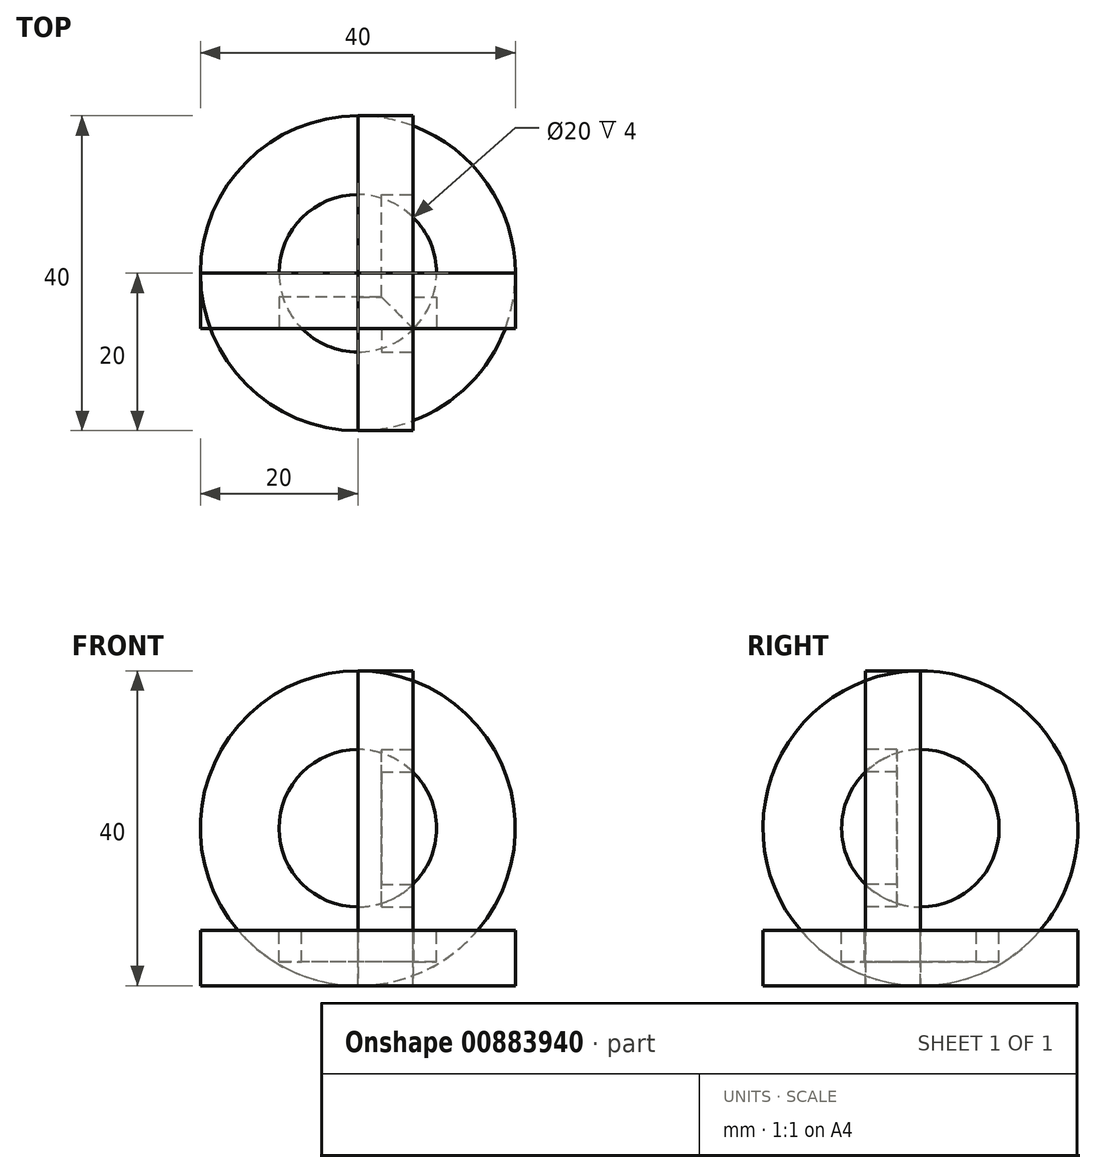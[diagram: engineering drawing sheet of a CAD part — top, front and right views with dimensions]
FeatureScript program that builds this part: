
annotation { "Feature Type Name" : "Feature", "Feature Type Description" : "" }
export const myFeature = defineFeature(function(context is Context, id is Id, definition is map)
    precondition{}
    {
        {
            assignVariable(context, id + "F0", {"name" : "outer_high", "anyValue" : 7});
        }
        {
            assignVariable(context, id + "F1", {"name" : "inner_high", "anyValue" : 4});
        }
        {
            assignVariable(context, id + "F2", {"name" : "column_angle", "anyValue" : 90});
        }
        {
            var Q0;
            Q0=qCreatedBy(makeId("Top.planeOp"),FACE);
            var sketch = newSketch(context, id + "F3", { "sketchPlane" : qUnion([Q0])});
            skCircle(sketch, "E0", {"center": v(0, 0) * mm, "radius": 20 * mm});
            skCircle(sketch, "E1", {"center": v(0, 0) * mm, "radius": 10 * mm});
            skSolve(sketch);
        }
        {
            var Q0;
            Q0=makeQuery(id+"F3.imprint","IMPRINT",FACE,{"disambiguationData":[TD([[makeQuery(id+"F3.imprint","IMPRINT",EDGE,{"derivedFrom":sQuery(id+"F3.wireOp",EDGE,"E0")}),1.0]])]});
            var Q1;
            Q1=makeQuery(id+"F3.imprint","IMPRINT",FACE,{"disambiguationData":[TD([[makeQuery(id+"F3.imprint","IMPRINT",EDGE,{"derivedFrom":sQuery(id+"F3.wireOp",EDGE,"E1")}),1.0]])]});
            extrude(context, id + "F4", {"entities" : qUnion([Q0, Q1]), "depth" : (getVariable(context, 'outer_high')) * mm, "offsetDistance" : 25 * mm});
        }
        {
            var Q0;
            Q0=makeQuery(id+"F4.opExtrude","CAP_FACE",FACE,{"disambiguationData":[OSD([sQuery(id+"F3.wireOp",EDGE,"E0")])],"isStart":false});
            var sketch = newSketch(context, id + "F5", { "sketchPlane" : qUnion([Q0])});
            skCircle(sketch, "E2.0", {"center": v(0, 0) * mm, "radius": 10 * mm});
            skSolve(sketch);
        }
        {
            var Q0;
            Q0=qCreatedBy(makeId("Front.planeOp"),FACE);
            var sketch = newSketch(context, id + "F6", { "sketchPlane" : qUnion([Q0])});
            skLineSegment(sketch, "E3", {"start": v(0, 70) * mm, "end": v(0, 0) * mm});
            skPoint(sketch, "E4", {"position": v(0, 20) * mm});
            skCircle(sketch, "E5", {"center": v(0, 20) * mm, "radius": 20 * mm});
            skCircle(sketch, "E6", {"center": v(0, 20) * mm, "radius": 10 * mm});
            skSolve(sketch);
        }
        {
            var Q0;
            {var subQ0=sQuery(id+"F6.wireOp",EDGE,"E5");var subQ1=sQuery(id+"F6.wireOp",EDGE,"E3");var subQ2=makeQuery(id+"F6.imprint","INTERSECT",VERTEX,{"disambiguationData":[OD(1.0)],"derivedFrom":[subQ1,subQ0]});Q0=makeQuery(id+"F6.imprint","IMPRINT",FACE,{"disambiguationData":[TD([[makeQuery(id+"F6.imprint","IMPRINT",EDGE,{"disambiguationData":[TD([[subQ2,-1.0]])],"derivedFrom":subQ1}),-1.0]])]});}
            var Q1;
            {var subQ0=sQuery(id+"F6.wireOp",EDGE,"E5");var subQ1=sQuery(id+"F6.wireOp",EDGE,"E3");var subQ2=makeQuery(id+"F6.imprint","INTERSECT",VERTEX,{"disambiguationData":[OD(1.0)],"derivedFrom":[subQ1,subQ0]});Q1=makeQuery(id+"F6.imprint","IMPRINT",FACE,{"disambiguationData":[TD([[makeQuery(id+"F6.imprint","IMPRINT",EDGE,{"disambiguationData":[TD([[subQ2,-1.0]])],"derivedFrom":subQ1}),1.0]])]});}
            var Q2;
            {var subQ0=sQuery(id+"F6.wireOp",EDGE,"E6");var subQ1=sQuery(id+"F6.wireOp",EDGE,"E3");var subQ2=makeQuery(id+"F6.imprint","INTERSECT",VERTEX,{"disambiguationData":[OD(0.0)],"derivedFrom":[subQ1,subQ0]});Q2=makeQuery(id+"F6.imprint","IMPRINT",FACE,{"disambiguationData":[TD([[makeQuery(id+"F6.imprint","IMPRINT",EDGE,{"disambiguationData":[TD([[subQ2,-1.0]])],"derivedFrom":subQ1}),-1.0]])]});}
            var Q3;
            {var subQ0=sQuery(id+"F6.wireOp",EDGE,"E6");var subQ1=sQuery(id+"F6.wireOp",EDGE,"E3");var subQ2=makeQuery(id+"F6.imprint","INTERSECT",VERTEX,{"disambiguationData":[OD(0.0)],"derivedFrom":[subQ1,subQ0]});Q3=makeQuery(id+"F6.imprint","IMPRINT",FACE,{"disambiguationData":[TD([[makeQuery(id+"F6.imprint","IMPRINT",EDGE,{"disambiguationData":[TD([[subQ2,-1.0]])],"derivedFrom":subQ1}),1.0]])]});}
            extrude(context, id + "F7", {"entities" : qUnion([Q0, Q1, Q2, Q3]), "depth" : (getVariable(context, 'outer_high')) * mm, "offsetDistance" : 25 * mm});
        }
        {
            var Q0;
            Q0=makeQuery(id+"F7.opExtrude","CAP_FACE",FACE,{"disambiguationData":[OSD([sQuery(id+"F6.wireOp",EDGE,"E5")])],"isStart":false});
            var sketch = newSketch(context, id + "F8", { "sketchPlane" : qUnion([Q0])});
            skCircle(sketch, "E7.0", {"center": v(0, 20) * mm, "radius": 10 * mm});
            skSolve(sketch);
        }
        {
            var Q0;
            Q0=sQuery(id+"F6.wireOp",EDGE,"E3");
            cPlane(context, id + "F9", {"entities" : qUnion([Q0]), "cplaneType" : CPlaneType.LINE_ANGLE, "offset" : 25 * mm, "angle" : (90 + getVariable(context, 'column_angle')) * degree, "oppositeDirection" : true, "width" : 150 * mm, "height" : 150 * mm});
        }
        {
            var Q0;
            Q0=qCreatedBy(id+"F9.planeOp",FACE);
            var sketch = newSketch(context, id + "F10", { "sketchPlane" : qUnion([Q0])});
            skCircle(sketch, "E8", {"center": v(0, 20) * mm, "radius": 20 * mm});
            skCircle(sketch, "E9", {"center": v(0, 20) * mm, "radius": 10 * mm});
            skSolve(sketch);
        }
        {
            var Q0;
            Q0=makeQuery(id+"F10.imprint","IMPRINT",FACE,{"disambiguationData":[TD([[makeQuery(id+"F10.imprint","IMPRINT",EDGE,{"derivedFrom":sQuery(id+"F10.wireOp",EDGE,"E8")}),1.0]])]});
            var Q1;
            Q1=makeQuery(id+"F10.imprint","IMPRINT",FACE,{"disambiguationData":[TD([[makeQuery(id+"F10.imprint","IMPRINT",EDGE,{"derivedFrom":sQuery(id+"F10.wireOp",EDGE,"E9")}),1.0]])]});
            extrude(context, id + "F11", {"entities" : qUnion([Q0, Q1]), "depth" : (getVariable(context, 'outer_high')) * mm, "offsetDistance" : 25 * mm});
        }
        {
            var Q0;
            Q0=makeQuery(id+"F11.opExtrude","CAP_FACE",FACE,{"disambiguationData":[OSD([sQuery(id+"F10.wireOp",EDGE,"E8")])],"isStart":false});
            var sketch = newSketch(context, id + "F12", { "sketchPlane" : qUnion([Q0])});
            skCircle(sketch, "E10.0", {"center": v(0, 20) * mm, "radius": 10 * mm});
            skSolve(sketch);
        }
        {
            var Q0;
            Q0=makeQuery(id+"F5.imprint","IMPRINT",FACE,{"disambiguationData":[TD([[makeQuery(id+"F5.imprint","IMPRINT",EDGE,{"derivedFrom":sQuery(id+"F5.wireOp",EDGE,"E2.0")}),1.0]])]});
            extrude(context, id + "F13", {"entities" : qUnion([Q0]), "operationType" : NewBodyOperationType.REMOVE, "oppositeDirection" : true, "depth" : (getVariable(context, 'inner_high')) * mm, "offsetDistance" : 25 * mm});
        }
        {
            var Q0;
            Q0=makeQuery(id+"F8.imprint","IMPRINT",FACE,{"disambiguationData":[TD([[makeQuery(id+"F8.imprint","IMPRINT",EDGE,{"derivedFrom":sQuery(id+"F8.wireOp",EDGE,"E7.0")}),1.0]])]});
            extrude(context, id + "F14", {"entities" : qUnion([Q0]), "operationType" : NewBodyOperationType.REMOVE, "oppositeDirection" : true, "depth" : (getVariable(context, 'inner_high')) * mm, "offsetDistance" : 25 * mm});
        }
        {
            var Q0;
            Q0=makeQuery(id+"F12.imprint","IMPRINT",FACE,{"disambiguationData":[TD([[makeQuery(id+"F12.imprint","IMPRINT",EDGE,{"derivedFrom":sQuery(id+"F12.wireOp",EDGE,"E10.0")}),1.0]])]});
            extrude(context, id + "F15", {"entities" : qUnion([Q0]), "operationType" : NewBodyOperationType.REMOVE, "oppositeDirection" : true, "depth" : (getVariable(context, 'inner_high')) * mm, "offsetDistance" : 25 * mm});
        }
    });
